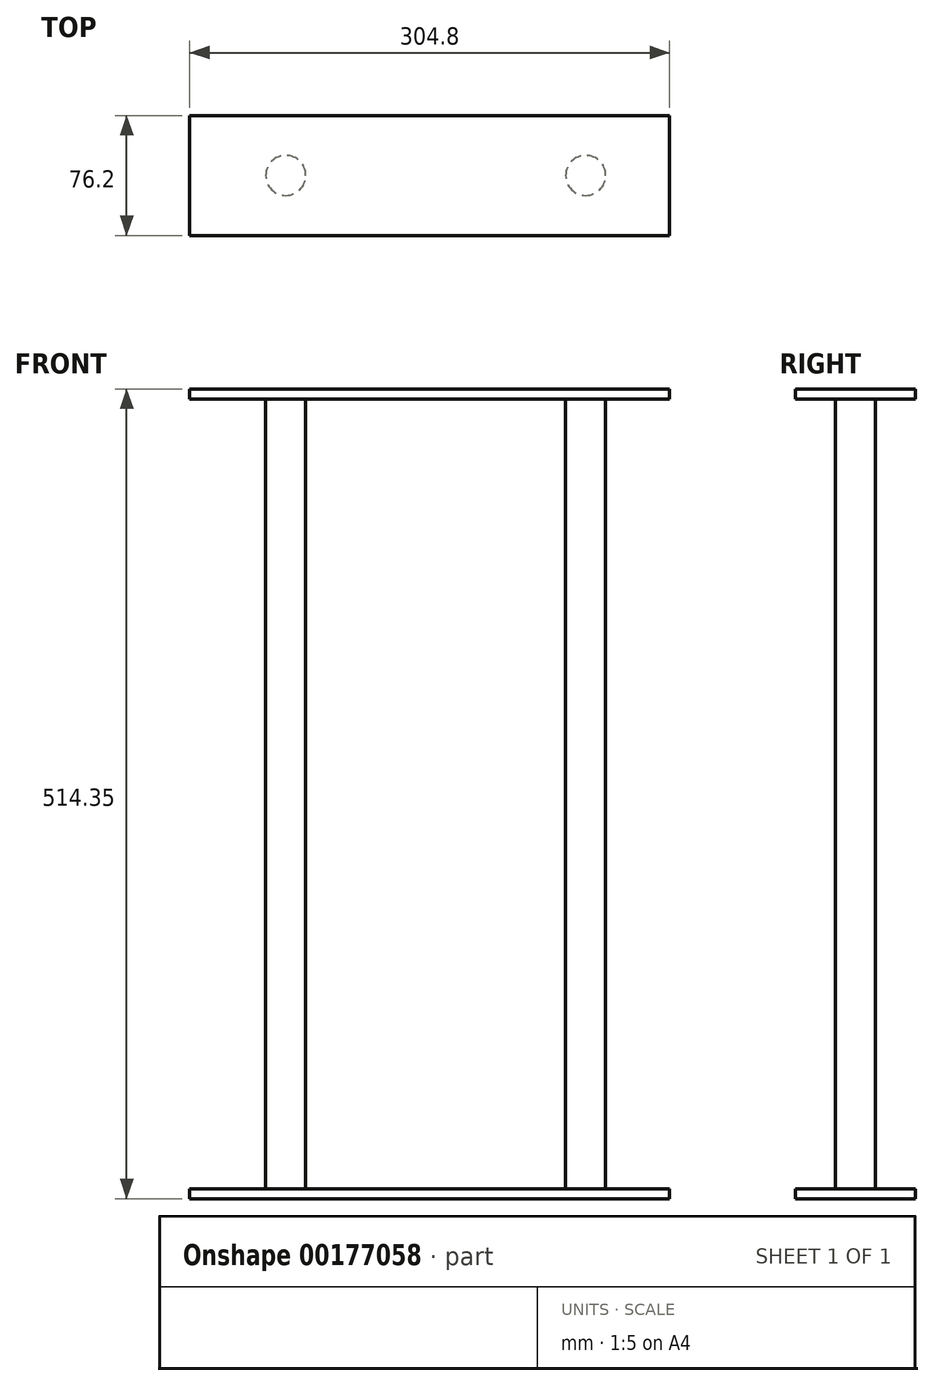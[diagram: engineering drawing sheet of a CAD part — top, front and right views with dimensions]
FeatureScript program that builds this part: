
annotation { "Feature Type Name" : "Feature", "Feature Type Description" : "" }
export const myFeature = defineFeature(function(context is Context, id is Id, definition is map)
    precondition{}
    {
        {
            var Q0;
            Q0=qCreatedBy(makeId("Top.planeOp"),FACE);
            var sketch = newSketch(context, id + "F0", { "sketchPlane" : qUnion([Q0])});
            skLineSegment(sketch, "E0.bottom", {"start": v(-152.4, 38.1) * mm, "end": v(152.4, 38.1) * mm});
            skLineSegment(sketch, "E0.top", {"start": v(-152.4, -38.1) * mm, "end": v(152.4, -38.1) * mm});
            skLineSegment(sketch, "E0.left", {"start": v(-152.4, 38.1) * mm, "end": v(-152.4, -38.1) * mm});
            skLineSegment(sketch, "E0.right", {"start": v(152.4, 38.1) * mm, "end": v(152.4, -38.1) * mm});
            skSolve(sketch);
        }
        {
            var Q0;
            Q0=makeQuery(id+"F0.imprint","IMPRINT",FACE,{"disambiguationData":[TD([[makeQuery(id+"F0.imprint","IMPRINT",EDGE,{"derivedFrom":sQuery(id+"F0.wireOp",EDGE,"E0.bottom")}),-1.0]])]});
            extrude(context, id + "F1", {"entities" : qUnion([Q0]), "depth" : 6.35 * mm});
        }
        {
            var Q0;
            Q0=makeQuery(id+"F1.opExtrude","CAP_FACE",FACE,{"disambiguationData":[OSD([sQuery(id+"F0.wireOp",EDGE,"E0.bottom"),sQuery(id+"F0.wireOp",EDGE,"E0.top"),sQuery(id+"F0.wireOp",EDGE,"E0.left"),sQuery(id+"F0.wireOp",EDGE,"E0.right")])],"isStart":false});
            var sketch = newSketch(context, id + "F2", { "sketchPlane" : qUnion([Q0])});
            skCircle(sketch, "E1", {"center": v(-91.44, 0) * mm, "radius": 12.7 * mm});
            skCircle(sketch, "E2", {"center": v(99.06, 0) * mm, "radius": 12.7 * mm});
            skSolve(sketch);
        }
        {
            var Q0;
            Q0 = qSketchRegion(id + "F2", true);
            extrude(context, id + "F3", {"entities" : qUnion([Q0]), "operationType" : NewBodyOperationType.ADD, "depth" : 508 * mm});
        }
        {
            var Q0;
            Q0=makeQuery(id+"F3.opExtrude","CAP_FACE",FACE,{"disambiguationData":[OSD([sQuery(id+"F2.wireOp",EDGE,"E1")])],"isStart":false});
            var sketch = newSketch(context, id + "F4", { "sketchPlane" : qUnion([Q0])});
            skLineSegment(sketch, "E3.bottom", {"start": v(-152.4, 38.1) * mm, "end": v(152.4, 38.1) * mm});
            skLineSegment(sketch, "E3.top", {"start": v(-152.4, -38.1) * mm, "end": v(152.4, -38.1) * mm});
            skLineSegment(sketch, "E3.left", {"start": v(-152.4, 38.1) * mm, "end": v(-152.4, -38.1) * mm});
            skLineSegment(sketch, "E3.right", {"start": v(152.4, 38.1) * mm, "end": v(152.4, -38.1) * mm});
            skSolve(sketch);
        }
        {
            var Q0;
            Q0=makeQuery(id+"F4.imprint","IMPRINT",FACE,{"disambiguationData":[TD([[makeQuery(id+"F4.imprint","IMPRINT",EDGE,{"derivedFrom":sQuery(id+"F4.wireOp",EDGE,"E3.bottom")}),-1.0]])]});
            extrude(context, id + "F5", {"entities" : qUnion([Q0]), "operationType" : NewBodyOperationType.ADD, "oppositeDirection" : true, "depth" : 6.35 * mm});
        }
    });
